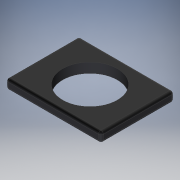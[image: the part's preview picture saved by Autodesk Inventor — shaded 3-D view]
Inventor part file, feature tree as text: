
AUTODESK INVENTOR PART (.ipt)
format: ipt  version: 2018 (Build 220112000, 112)  size: 132,608 bytes
history: native  units: mm
features: fillet x2, extrude x1
ambient origin geometry x8: Origin, YZ Plane, XZ Plane, XY Plane, X Axis, Y Axis, Z Axis, Center Point
bodies: Solid1 (feature_tree)
feature tree (3):
  extrude  "Extrusion1"  Depth=11.2mm
  fillet  "Fillet1"  Radius=2.0mm
  fillet  "Fillet2"  Radius=0.5mm
